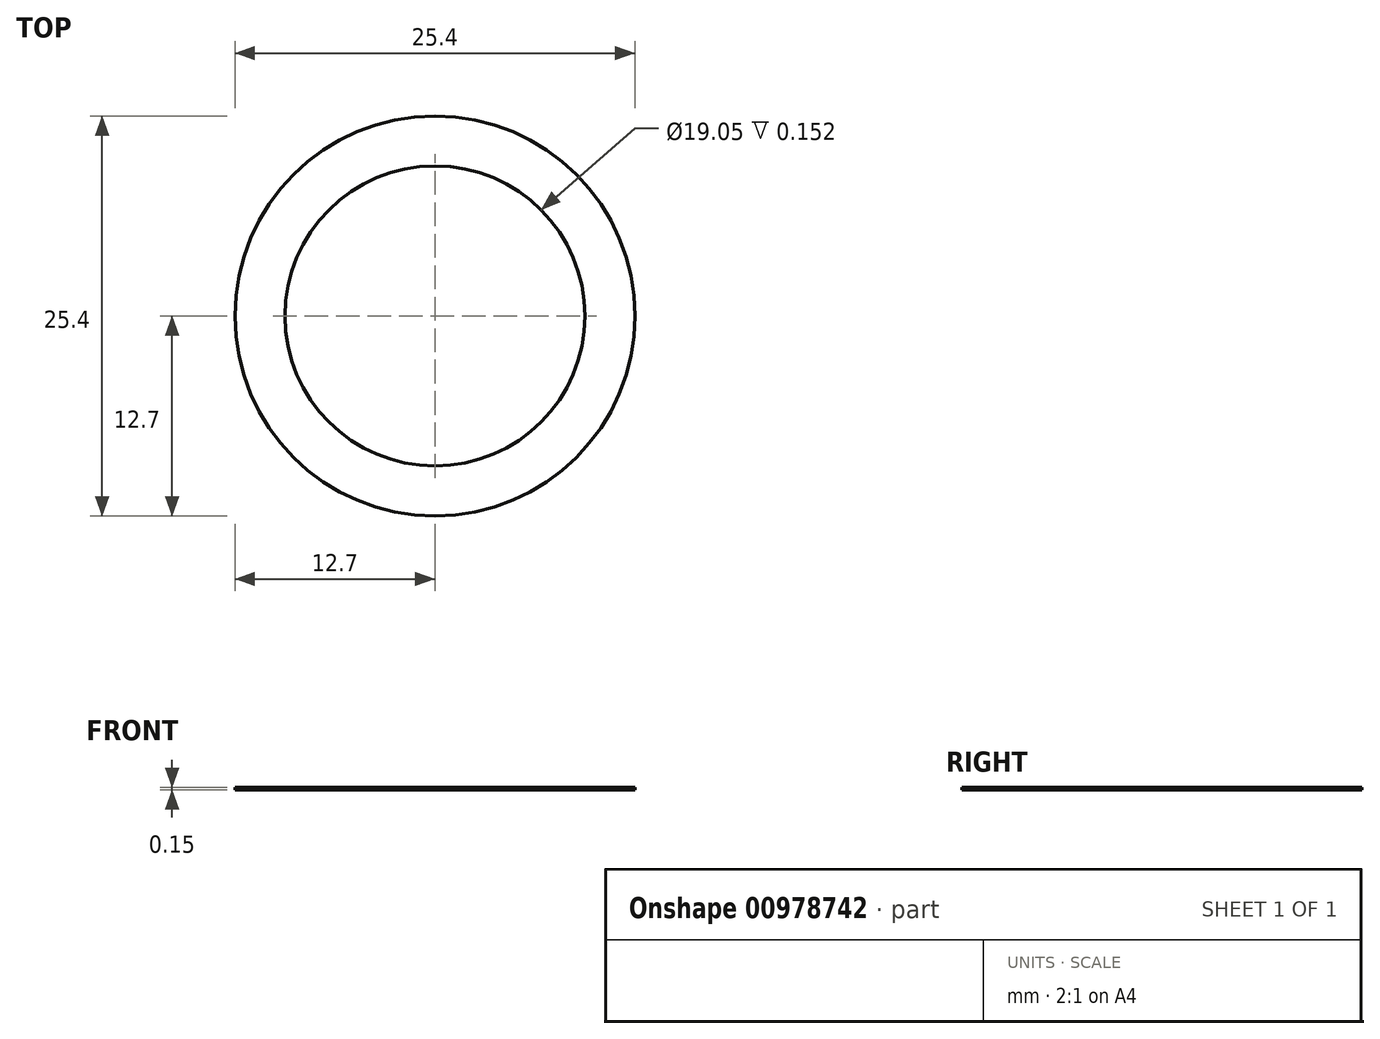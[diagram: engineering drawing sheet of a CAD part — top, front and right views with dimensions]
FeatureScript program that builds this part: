
annotation { "Feature Type Name" : "Feature", "Feature Type Description" : "" }
export const myFeature = defineFeature(function(context is Context, id is Id, definition is map)
    precondition{}
    {
        {
            var Q0;
            Q0=qCreatedBy(makeId("Top.planeOp"),FACE);
            var sketch = newSketch(context, id + "F0", { "sketchPlane" : qUnion([Q0])});
            skCircle(sketch, "E0", {"center": v(0, 0) * mm, "radius": 12.7 * mm});
            skCircle(sketch, "E1", {"center": v(0, 0) * mm, "radius": 9.53 * mm});
            skSolve(sketch);
        }
        {
            var Q0;
            Q0=makeQuery(id+"F0.imprint","IMPRINT",FACE,{"disambiguationData":[TD([[makeQuery(id+"F0.imprint","IMPRINT",EDGE,{"derivedFrom":sQuery(id+"F0.wireOp",EDGE,"E0")}),1.0]])]});
            extrude(context, id + "F1", {"entities" : qUnion([Q0]), "depth" : 0.15 * mm, "offsetDistance" : 25.4 * mm});
        }
    });
